# Revit family: Gira_029003
name_source: partatom
category: Elektroinstallationen
revit_build: Autodesk Revit 2017 (Build: 20160225_1515(x64)
units: mm (PartAtom-declared; Revit-internal decimal feet)

## family parameters
Basisbauteil = Fläche
Beim Laden mit Abzugskörper schneiden = Nein
Bemaßung runder Anschluss = Durchmesser verwenden
Beschriftungsausrichtung beibehalten = Nein
Gemeinsam genutzt = Nein
Raumberechnungspunkt = Nein
Teiletyp = Normal

## types (1)
- Gira_029003
    Acoustic signal = Ja
    Analogue input = Nein
    BIM = https://media.stage.bim.site und Tasten.rfa
    Beschreibung = Rock.ctrl.w. Sys55 PW,Rocker with control window,,pure white glossy,
    Bus connection included = Nein
    Bus system KNX = Ja
    Bus system KNX radio = Nein
    Bus system LON = Nein
    Bus system Powernet = Nein
    Bus system radio frequent = Nein
    Colour = White
    Data sheet = https://katalog.gira.de
    Degree of protection (IP) = IP20
    GTIN = 4010337290032
    HAN = 029003
    Halogen free = Ja
    Hersteller = Gira
    Imprint/indication = Without imprint
    Material = Plastic
    Material quality = Thermoplastic
    Model = Single rocker
    Monitoring window/light outlet = Ja
    Mounting method = Flush mounted (plaster)
    Number of channels = 3
    Other bus systems = None
    Productwebsite = http://katalog.gira.de
    RAL-number (akin) = 9010
    Scannable symbol / barrier free = Nein
    Suitable for degree of protection (IP) = IP20
    Suitable for touch sensor connector for bus system = Nein
    Surface finishing = Glossy
    Surface protection = Other
    Transparent = Nein
    Type of fastening = Clamp mounting
    Typname = Rocker ctrl.win. System 55 p.white
    URL = https://www.gira.de
    Utilization = Switch/push button
    Vorgabe-Ansicht = 1219 mm
    Weather station = Nein
    With DCF77 = Nein
    With exchangeable lens/symbol = Nein
    With heating = Nein
    With label area = Nein

## geometry (parser evidence)
native form markers: Sweep x7
no freeform markers — native parametric forms only
